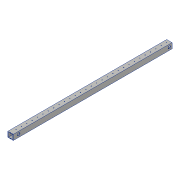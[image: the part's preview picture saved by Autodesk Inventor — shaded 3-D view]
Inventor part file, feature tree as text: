
AUTODESK INVENTOR PART (.ipt)
format: ipt  version: 2018 (Build 220112000, 112)  size: 161,280 bytes
history: native  units: in
note: dims shown in document units (in); Inventor stores cm internally (conversion verified against a paired STEP export)
features: sketch x3, hole x2, extrude x1, shell x1
ambient origin geometry x8: Origin, YZ Plane, XZ Plane, XY Plane, X Axis, Y Axis, Z Axis, Center Point
bodies: Solid1 (feature_tree)
feature tree (7):
  extrude  "Extrusion1"  Depth=1.0in
  shell  "Shell1"  Thickness=29.5in
  hole  "Hole1"  [1 undecoded]
  hole  "Hole5"  [1 undecoded]
  sketch  "Sketch1"  dims[d0=1.0in d1=1.0in d2=29.5in d3=0.0in]
  sketch  "Sketch2"  dims[d4=0.1in d5=0.5in]
  sketch  "Sketch8"  dims[d6=0.5in d7=14.5669in d9=1.0in d10=0.3937in d12=1.0in d14=0.1in d15=0.75in d16=0.375in d17=0.25in d18=0.5635in d19=2.0in d20=0.8108in d57=1.0in d58=0.5in d59=0.5in d60=0.5in d61=0.5in d62=0.75in d63=0.375in d64=0.25in d65=0.5635in d66=1.0in d67=0.8108in]
note: 2 required parameter values undecoded (feature->parameter linkage not recoverable at this tier; creation-order binding heuristic only, values carry confidence <= 0.55)
